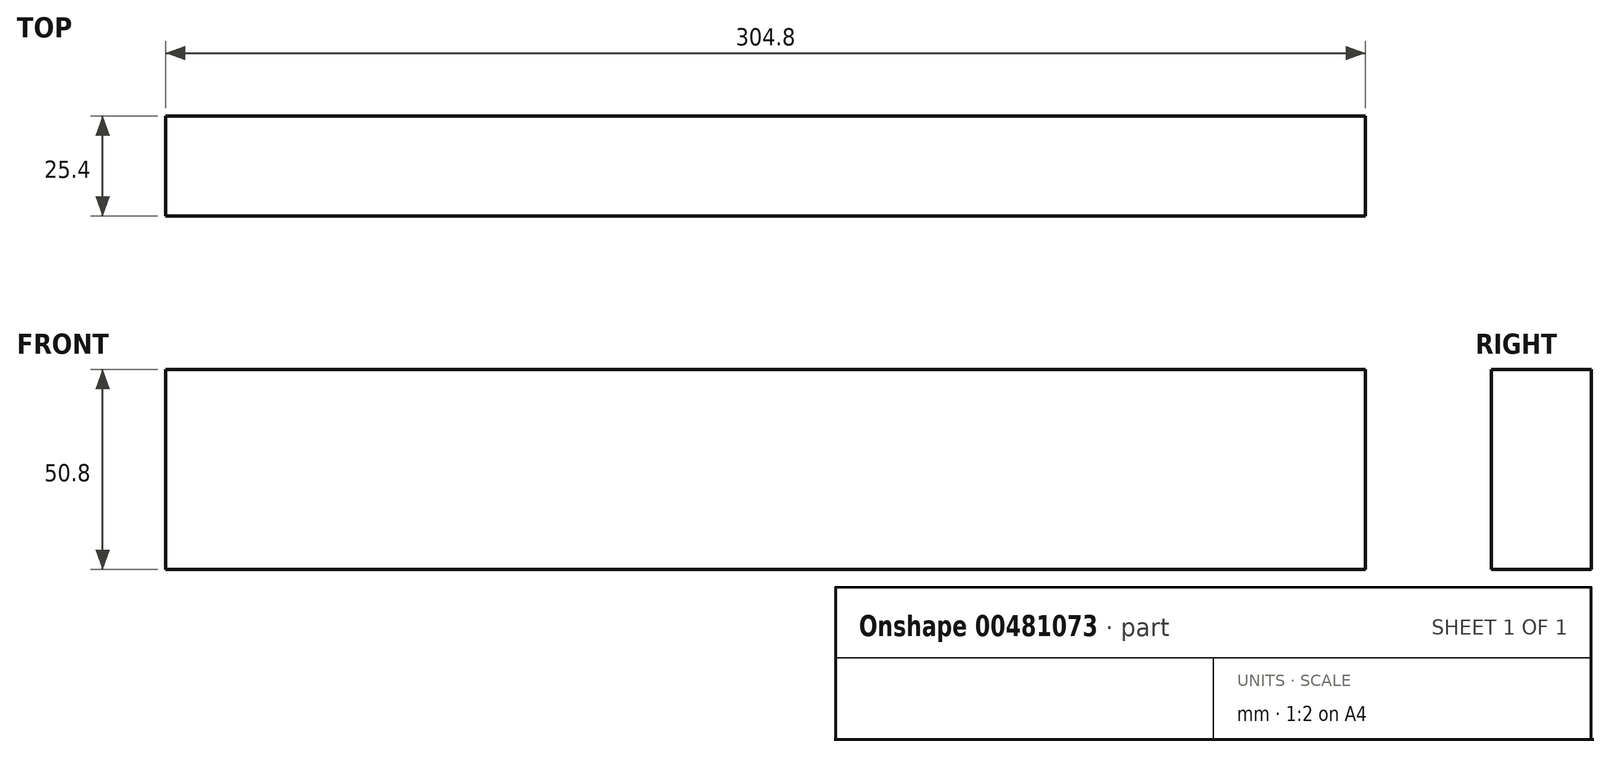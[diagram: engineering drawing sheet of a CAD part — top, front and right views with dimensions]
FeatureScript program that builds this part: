
annotation { "Feature Type Name" : "Feature", "Feature Type Description" : "" }
export const myFeature = defineFeature(function(context is Context, id is Id, definition is map)
    precondition{}
    {
        {
            var Q0;
            Q0=qCreatedBy(makeId("Top.planeOp"),FACE);
            var sketch = newSketch(context, id + "F0", { "sketchPlane" : qUnion([Q0])});
            skLineSegment(sketch, "E0.bottom", {"start": v(0, 0) * mm, "end": v(-304.8, 0) * mm});
            skLineSegment(sketch, "E0.top", {"start": v(0, 25.4) * mm, "end": v(-304.8, 25.4) * mm});
            skLineSegment(sketch, "E0.left", {"start": v(0, 0) * mm, "end": v(0, 25.4) * mm});
            skLineSegment(sketch, "E0.right", {"start": v(-304.8, 0) * mm, "end": v(-304.8, 25.4) * mm});
            skSolve(sketch);
        }
        {
            var Q0;
            Q0=makeQuery(id+"F0.imprint","IMPRINT",FACE,{"disambiguationData":[TD([[makeQuery(id+"F0.imprint","IMPRINT",EDGE,{"derivedFrom":sQuery(id+"F0.wireOp",EDGE,"E0.bottom")}),-1.0]])]});
            extrude(context, id + "F1", {"entities" : qUnion([Q0]), "depth" : 50.8 * mm});
        }
    });
